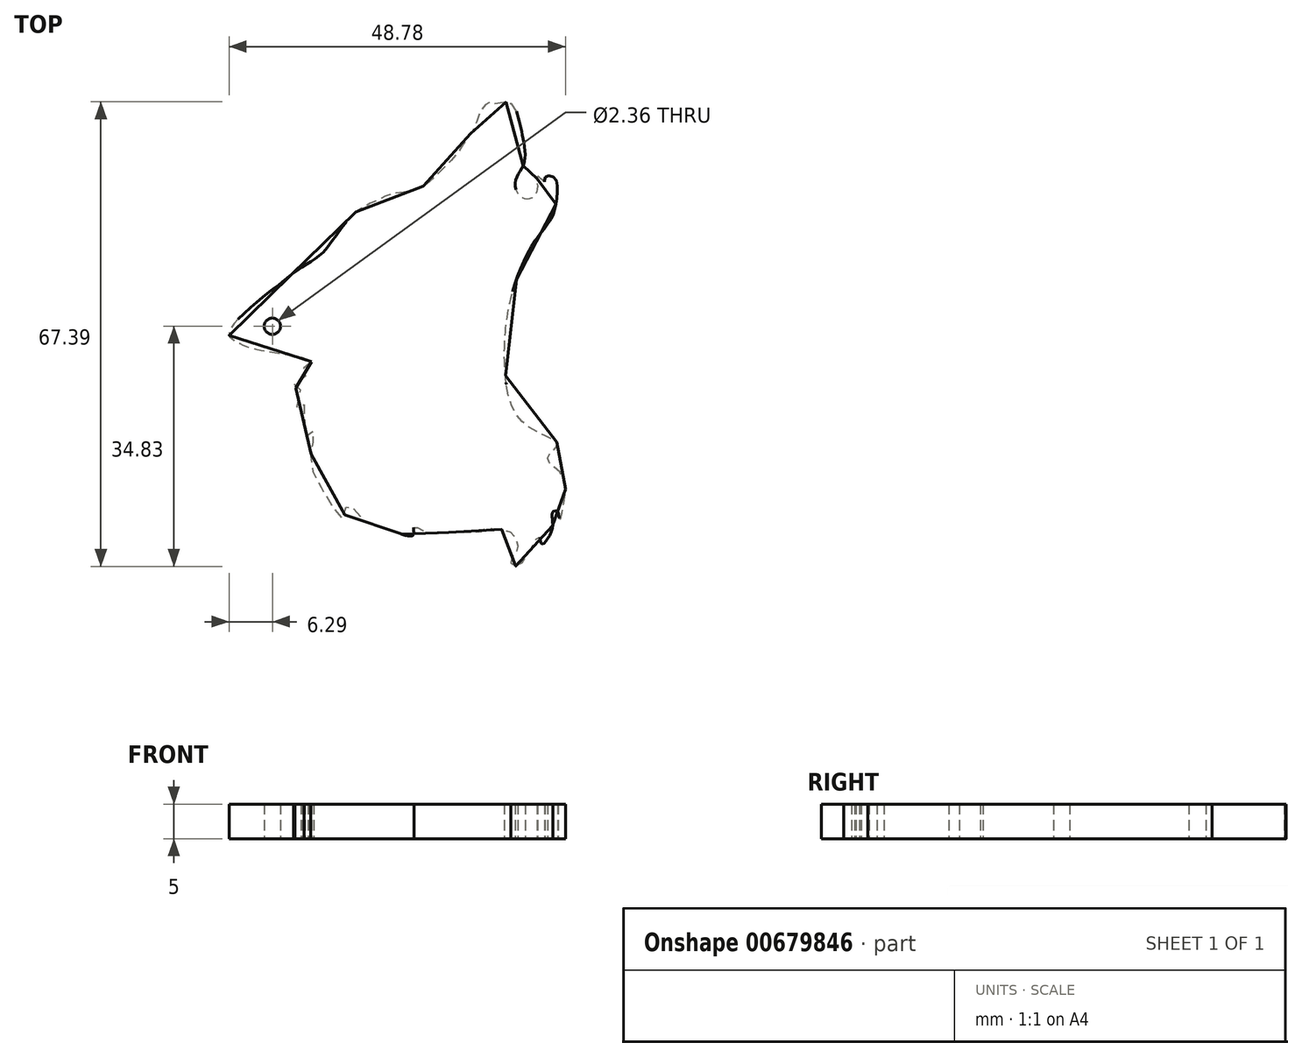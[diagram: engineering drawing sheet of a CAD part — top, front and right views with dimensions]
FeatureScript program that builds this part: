
annotation { "Feature Type Name" : "Feature", "Feature Type Description" : "" }
export const myFeature = defineFeature(function(context is Context, id is Id, definition is map)
    precondition{}
    {
        {
            var Q0;
            Q0=qCreatedBy(makeId("Top.planeOp"),FACE);
            var sketch = newSketch(context, id + "F0", { "sketchPlane" : qUnion([Q0])});
            skFitSpline(sketch, "E0", {"points": [v(-46.32, 34.92) * mm, v(-47.44, 33.96) * mm, v(-47.8, 33.44) * mm, v(-46.84, 33.29) * mm, v(-47.96, 32.33) * mm, v(-48.85, 31.29) * mm, v(-47.58, 30.54) * mm, v(-48.7, 28.99) * mm, v(-48.1, 28.32) * mm, v(-47.36, 28.69) * mm, v(-47.36, 24.9) * mm, v(-46.77, 23.8) * mm, v(-46.32, 25.2) * mm, v(-46.03, 24.54) * mm, v(-46.25, 22.6) * mm, v(-46.25, 19.5) * mm, v(-44.02, 15.19) * mm, v(-41.72, 12.22) * mm, v(-41.06, 14.3) * mm, v(-39.05, 12.15) * mm, v(-35.34, 10.66) * mm, v(-31.56, 9.77) * mm, v(-31.49, 10.96) * mm, v(-30.08, 10.37) * mm, v(-27.48, 10.07) * mm, v(-24.96, 10.22) * mm, v(-22.8, 10.22) * mm, v(-21.62, 10.3) * mm, v(-21.4, 10.59) * mm, v(-18.58, 10.59) * mm, v(-16.8, 9.55) * mm, v(-16.5, 7.47) * mm, v(-17.24, 6.58) * mm, v(-17.24, 5.47) * mm, v(-15.83, 5.7) * mm, v(-13.3, 9.62) * mm, v(-12.94, 8.51) * mm, v(-11.38, 10.89) * mm, v(-11.38, 13.04) * mm, v(-10.64, 13.18) * mm, v(-10.34, 12) * mm, v(-9.6, 15.26) * mm, v(-10.12, 18.75) * mm, v(-12.05, 20.68) * mm, v(-11.16, 22.24) * mm, v(-10.57, 22.98) * mm, v(-12.57, 24.24) * mm, v(-16.57, 27.13) * mm, v(-18.28, 34.03) * mm, v(-18.06, 40.56) * mm, v(-16.86, 46.02) * mm, v(-14.13, 52.11) * mm, v(-11.54, 55.68) * mm, v(-10.77, 58.49) * mm, v(-11.12, 61.64) * mm, v(-12.45, 61.64) * mm, v(-12.52, 61) * mm, v(-13.5, 61.78) * mm, v(-13.64, 59.68) * mm, v(-15.46, 58.56) * mm, v(-16.8, 60.87) * mm, v(-15.53, 63.6) * mm, v(-15.67, 67.45) * mm, v(-16.46, 70.82) * mm, v(-17.75, 72.52) * mm, v(-19.98, 72.37) * mm, v(-20.28, 72.62) * mm, v(-21.57, 71.68) * mm, v(-22.6, 69.06) * mm, v(-23.8, 67.27) * mm, v(-25.33, 64.95) * mm, v(-27.9, 62.27) * mm, v(-31.07, 59.9) * mm, v(-35.23, 59.15) * mm, v(-36.02, 58.66) * mm, v(-39.64, 56.83) * mm, v(-44.54, 50.89) * mm, v(-47.26, 48.95) * mm, v(-50.88, 46.23) * mm, v(-53.4, 44.25) * mm, v(-58.26, 39.15) * mm, v(-57.36, 37.91) * mm, v(-53.55, 36.58) * mm, v(-46.32, 34.92) * mm]});
            skCircle(sketch, "E1", {"center": v(-51.98, 40.07) * mm, "radius": 1.18 * mm});
            skSolve(sketch);
        }
        {
            var Q0;
            Q0=makeQuery(id+"F0.imprint","IMPRINT",FACE,{"disambiguationData":[TD([[makeQuery(id+"F0.imprint","IMPRINT",EDGE,{"derivedFrom":sQuery(id+"F0.wireOp",EDGE,"E0")}),1.0]])]});
            extrude(context, id + "F1", {"entities" : qUnion([Q0]), "depth" : 5 * mm, "offsetDistance" : 25 * mm});
        }
    });
